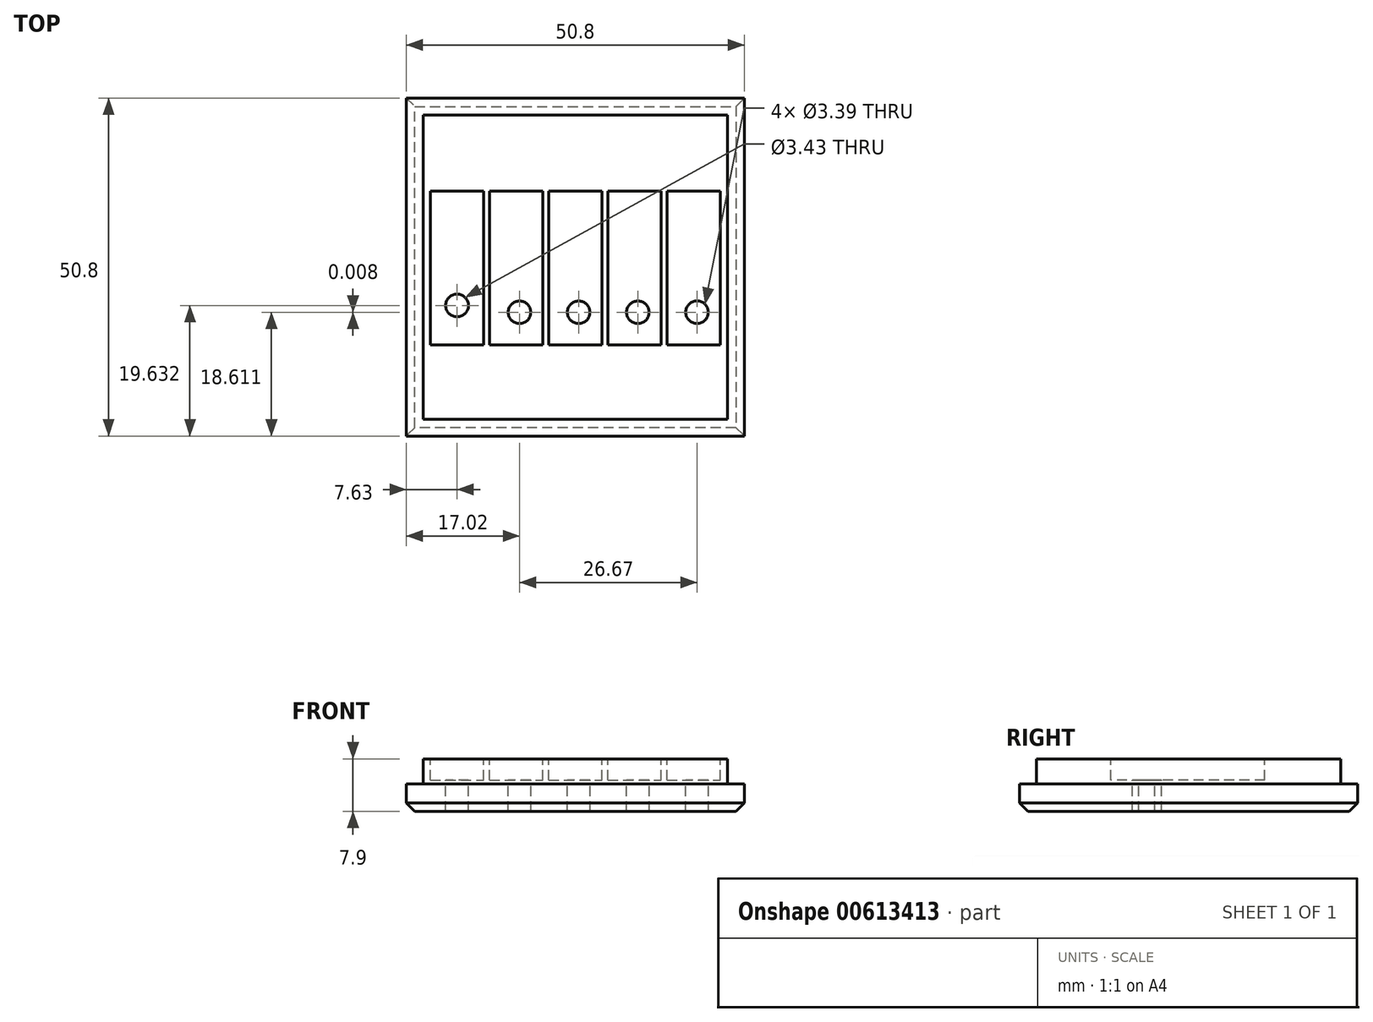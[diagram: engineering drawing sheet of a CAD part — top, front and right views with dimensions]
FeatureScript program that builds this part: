
annotation { "Feature Type Name" : "Feature", "Feature Type Description" : "" }
export const myFeature = defineFeature(function(context is Context, id is Id, definition is map)
    precondition{}
    {
        {
            var Q0;
            Q0=qCreatedBy(makeId("Top.planeOp"),FACE);
            var sketch = newSketch(context, id + "F0", { "sketchPlane" : qUnion([Q0])});
            skLineSegment(sketch, "E0.bottom", {"start": v(-12.32, 40.12) * mm, "end": v(38.48, 40.12) * mm});
            skLineSegment(sketch, "E0.top", {"start": v(-12.32, -10.68) * mm, "end": v(38.48, -10.68) * mm});
            skLineSegment(sketch, "E0.left", {"start": v(-12.32, 40.12) * mm, "end": v(-12.32, -10.68) * mm});
            skLineSegment(sketch, "E0.right", {"start": v(38.48, 40.12) * mm, "end": v(38.48, -10.68) * mm});
            skSolve(sketch);
        }
        {
            var Q0;
            Q0=makeQuery(id+"F0.imprint","IMPRINT",FACE,{"disambiguationData":[TD([[makeQuery(id+"F0.imprint","IMPRINT",EDGE,{"derivedFrom":sQuery(id+"F0.wireOp",EDGE,"E0.bottom")}),-1.0]])]});
            extrude(context, id + "F1", {"entities" : qUnion([Q0]), "depth" : 4.13 * mm, "offsetDistance" : 25.4 * mm});
        }
        {
            var Q0;
            Q0=makeQuery(id+"F1.opExtrude","CAP_FACE",FACE,{"disambiguationData":[OSD([sQuery(id+"F0.wireOp",EDGE,"E0.bottom"),sQuery(id+"F0.wireOp",EDGE,"E0.top"),sQuery(id+"F0.wireOp",EDGE,"E0.left"),sQuery(id+"F0.wireOp",EDGE,"E0.right")])],"isStart":true});
            var sketch = newSketch(context, id + "F2", { "sketchPlane" : qUnion([Q0])});
            skLineSegment(sketch, "E1.bottom", {"start": v(-10.03, 8.4) * mm, "end": v(36.2, 8.4) * mm});
            skLineSegment(sketch, "E1.top", {"start": v(-10.03, -37.84) * mm, "end": v(36.2, -37.84) * mm});
            skLineSegment(sketch, "E1.left", {"start": v(-10.03, 8.4) * mm, "end": v(-10.03, -37.84) * mm});
            skLineSegment(sketch, "E1.right", {"start": v(36.2, 8.4) * mm, "end": v(36.2, -37.84) * mm});
            skSolve(sketch);
        }
        {
            var Q0;
            Q0=makeQuery(id+"F1.opExtrude","CAP_FACE",FACE,{"disambiguationData":[OSD([sQuery(id+"F0.wireOp",EDGE,"E0.bottom"),sQuery(id+"F0.wireOp",EDGE,"E0.top"),sQuery(id+"F0.wireOp",EDGE,"E0.left"),sQuery(id+"F0.wireOp",EDGE,"E0.right")])],"isStart":false});
            var sketch = newSketch(context, id + "F3", { "sketchPlane" : qUnion([Q0])});
            skLineSegment(sketch, "E2.bottom", {"start": v(-9.78, 37.58) * mm, "end": v(35.94, 37.58) * mm});
            skLineSegment(sketch, "E2.top", {"start": v(-9.78, -8.14) * mm, "end": v(35.94, -8.14) * mm});
            skLineSegment(sketch, "E2.left", {"start": v(-9.78, 37.58) * mm, "end": v(-9.78, -8.14) * mm});
            skLineSegment(sketch, "E2.right", {"start": v(35.94, 37.58) * mm, "end": v(35.94, -8.14) * mm});
            skSolve(sketch);
        }
        {
            var Q0;
            Q0=makeQuery(id+"F3.imprint","IMPRINT",FACE,{"disambiguationData":[TD([[makeQuery(id+"F3.imprint","IMPRINT",EDGE,{"derivedFrom":sQuery(id+"F3.wireOp",EDGE,"E2.bottom")}),-1.0]])]});
            extrude(context, id + "F4", {"entities" : qUnion([Q0]), "operationType" : NewBodyOperationType.ADD, "depth" : 3.77 * mm, "offsetDistance" : 25.4 * mm});
        }
        {
            var Q0;
            Q0=makeQuery(id+"F4.opExtrude","CAP_FACE",FACE,{"disambiguationData":[OSD([sQuery(id+"F3.wireOp",EDGE,"E2.bottom"),sQuery(id+"F3.wireOp",EDGE,"E2.top"),sQuery(id+"F3.wireOp",EDGE,"E2.left"),sQuery(id+"F3.wireOp",EDGE,"E2.right")])],"isStart":false});
            var sketch = newSketch(context, id + "F5", { "sketchPlane" : qUnion([Q0])});
            skLineSegment(sketch, "E3.bottom", {"start": v(-8.69, 26.15) * mm, "end": v(-0.69, 26.15) * mm});
            skLineSegment(sketch, "E3.top", {"start": v(-8.69, 3.04) * mm, "end": v(-0.69, 3.04) * mm});
            skLineSegment(sketch, "E3.left", {"start": v(-8.69, 26.15) * mm, "end": v(-8.69, 3.04) * mm});
            skLineSegment(sketch, "E3.right", {"start": v(-0.69, 26.15) * mm, "end": v(-0.69, 3.04) * mm});
            skLineSegment(sketch, "E4.1.0.0", {"start": v(0.2, 26.15) * mm, "end": v(0.2, 3.04) * mm});
            skLineSegment(sketch, "E4.1.0.1", {"start": v(8.2, 26.15) * mm, "end": v(8.2, 3.04) * mm});
            skLineSegment(sketch, "E4.1.0.2", {"start": v(0.2, 26.15) * mm, "end": v(8.2, 26.15) * mm});
            skLineSegment(sketch, "E4.1.0.3", {"start": v(0.2, 3.04) * mm, "end": v(8.2, 3.04) * mm});
            skLineSegment(sketch, "E4.2.0.0", {"start": v(9.1, 26.15) * mm, "end": v(9.1, 3.04) * mm});
            skLineSegment(sketch, "E4.2.0.1", {"start": v(17.1, 26.15) * mm, "end": v(17.1, 3.04) * mm});
            skLineSegment(sketch, "E4.2.0.2", {"start": v(9.1, 26.15) * mm, "end": v(17.1, 26.15) * mm});
            skLineSegment(sketch, "E4.2.0.3", {"start": v(9.1, 3.04) * mm, "end": v(17.1, 3.04) * mm});
            skLineSegment(sketch, "E4.direction1", {"start": v(-8.69, 3.04) * mm, "end": v(0.2, 3.04) * mm, "construction": true});
            skLineSegment(sketch, "E4.direction2", {"start": v(-8.69, 3.04) * mm, "end": v(-8.69, 32.5) * mm, "construction": true});
            skLineSegment(sketch, "E5.0.3.0", {"start": v(17.98, 26.15) * mm, "end": v(17.98, 3.04) * mm});
            skLineSegment(sketch, "E5.3.3.0", {"start": v(25.98, 26.15) * mm, "end": v(25.98, 3.04) * mm});
            skLineSegment(sketch, "E5.6.3.0", {"start": v(17.98, 26.15) * mm, "end": v(25.98, 26.15) * mm});
            skLineSegment(sketch, "E5.9.3.0", {"start": v(17.98, 3.04) * mm, "end": v(25.98, 3.04) * mm});
            skLineSegment(sketch, "E5.0.4.0", {"start": v(26.87, 26.15) * mm, "end": v(26.87, 3.04) * mm});
            skLineSegment(sketch, "E5.3.4.0", {"start": v(34.87, 26.15) * mm, "end": v(34.87, 3.04) * mm});
            skLineSegment(sketch, "E5.6.4.0", {"start": v(26.87, 26.15) * mm, "end": v(34.87, 26.15) * mm});
            skLineSegment(sketch, "E5.9.4.0", {"start": v(26.87, 3.04) * mm, "end": v(34.87, 3.04) * mm});
            skSolve(sketch);
        }
        {
            var Q0;
            Q0=makeQuery(id+"F5.imprint","IMPRINT",FACE,{"disambiguationData":[TD([[makeQuery(id+"F5.imprint","IMPRINT",EDGE,{"derivedFrom":sQuery(id+"F5.wireOp",EDGE,"E4.1.0.0")}),1.0]])]});
            var Q1;
            Q1=makeQuery(id+"F5.imprint","IMPRINT",FACE,{"disambiguationData":[TD([[makeQuery(id+"F5.imprint","IMPRINT",EDGE,{"derivedFrom":sQuery(id+"F5.wireOp",EDGE,"E4.2.0.0")}),1.0]])]});
            var Q2;
            Q2=makeQuery(id+"F5.imprint","IMPRINT",FACE,{"disambiguationData":[TD([[makeQuery(id+"F5.imprint","IMPRINT",EDGE,{"derivedFrom":sQuery(id+"F5.wireOp",EDGE,"E5.0.3.0")}),1.0]])]});
            var Q3;
            Q3=makeQuery(id+"F5.imprint","IMPRINT",FACE,{"disambiguationData":[TD([[makeQuery(id+"F5.imprint","IMPRINT",EDGE,{"derivedFrom":sQuery(id+"F5.wireOp",EDGE,"E5.0.4.0")}),1.0]])]});
            var Q4;
            Q4=makeQuery(id+"F5.imprint","IMPRINT",FACE,{"disambiguationData":[TD([[makeQuery(id+"F5.imprint","IMPRINT",EDGE,{"derivedFrom":sQuery(id+"F5.wireOp",EDGE,"E3.bottom")}),-1.0]])]});
            extrude(context, id + "F6", {"entities" : qUnion([Q0, Q1, Q2, Q3, Q4]), "operationType" : NewBodyOperationType.REMOVE, "oppositeDirection" : true, "depth" : 3.2 * mm, "offsetDistance" : 25.4 * mm});
        }
        {
            var Q0;
            Q0=makeQuery(id+"F6.boolean.opBoolean","COPY",FACE,{"derivedFrom":makeQuery(id+"F6.opExtrude","CAP_FACE",FACE,{"disambiguationData":[OSD([sQuery(id+"F5.wireOp",EDGE,"E3.bottom"),sQuery(id+"F5.wireOp",EDGE,"E3.top"),sQuery(id+"F5.wireOp",EDGE,"E3.left"),sQuery(id+"F5.wireOp",EDGE,"E3.right")])],"isStart":false})});
            var sketch = newSketch(context, id + "F7", { "sketchPlane" : qUnion([Q0])});
            skCircle(sketch, "E6", {"center": v(-4.69, 8.95) * mm, "radius": 1.71 * mm});
            skLineSegment(sketch, "E7.bottom", {"start": v(3.2, -6.76) * mm, "end": v(26.27, -6.76) * mm});
            skLineSegment(sketch, "E7.top", {"start": v(3.2, 1.24) * mm, "end": v(26.27, 1.24) * mm});
            skLineSegment(sketch, "E7.left", {"start": v(3.2, -6.76) * mm, "end": v(3.2, 1.24) * mm});
            skLineSegment(sketch, "E7.right", {"start": v(26.27, -6.76) * mm, "end": v(26.27, 1.24) * mm});
            skLineSegment(sketch, "E8.bottom", {"start": v(3.1, 3.08) * mm, "end": v(26.16, 3.08) * mm});
            skLineSegment(sketch, "E8.top", {"start": v(3.1, 11.08) * mm, "end": v(26.16, 11.08) * mm});
            skLineSegment(sketch, "E8.left", {"start": v(3.1, 3.08) * mm, "end": v(3.1, 11.08) * mm});
            skLineSegment(sketch, "E8.right", {"start": v(26.16, 3.08) * mm, "end": v(26.16, 11.08) * mm});
            skCircle(sketch, "E9", {"center": v(21.41, -2.74) * mm, "radius": 1.71 * mm});
            skCircle(sketch, "E10", {"center": v(21.31, 7.1) * mm, "radius": 1.71 * mm});
            skSolve(sketch);
        }
        {
            var Q0;
            Q0=makeQuery(id+"F7.imprint","IMPRINT",FACE,{"disambiguationData":[TD([[makeQuery(id+"F7.imprint","IMPRINT",EDGE,{"derivedFrom":sQuery(id+"F7.wireOp",EDGE,"E6")}),1.0]])]});
            var Q1;
            Q1=qSketchRegion(id+"F10",true);
            extrude(context, id + "F8", {"entities" : qUnion([Q0, Q1]), "operationType" : NewBodyOperationType.REMOVE, "oppositeDirection" : true, "depth" : 25.4 * mm, "offsetDistance" : 25.4 * mm});
        }
        {
            var Q0;
            Q0=makeQuery(id+"F1.opExtrude","CAP_EDGE",EDGE,{"disambiguationData":[OSD([sQuery(id+"F0.wireOp",EDGE,"E0.top")])],"isStart":true});
            var Q1;
            Q1=makeQuery(id+"F1.opExtrude","CAP_EDGE",EDGE,{"disambiguationData":[OSD([sQuery(id+"F0.wireOp",EDGE,"E0.bottom")])],"isStart":true});
            var Q2;
            Q2=makeQuery(id+"F1.opExtrude","CAP_EDGE",EDGE,{"disambiguationData":[OSD([sQuery(id+"F0.wireOp",EDGE,"E0.left")])],"isStart":true});
            var Q3;
            Q3=makeQuery(id+"F1.opExtrude","CAP_EDGE",EDGE,{"disambiguationData":[OSD([sQuery(id+"F0.wireOp",EDGE,"E0.right")])],"isStart":true});
            chamfer(context, id + "F9", {"entities" : qUnion([Q0, Q1, Q2, Q3]), "width" : 1.27 * mm, "tangentPropagation" : true});
        }
        {
            var Q0;
            Q0=makeQuery(id+"F6.boolean.opBoolean","COPY",FACE,{"derivedFrom":makeQuery(id+"F6.opExtrude","CAP_FACE",FACE,{"disambiguationData":[OSD([sQuery(id+"F5.wireOp",EDGE,"E4.1.0.0"),sQuery(id+"F5.wireOp",EDGE,"E4.1.0.1"),sQuery(id+"F5.wireOp",EDGE,"E4.1.0.2"),sQuery(id+"F5.wireOp",EDGE,"E4.1.0.3")])],"isStart":false})});
            var sketch = newSketch(context, id + "F10", { "sketchPlane" : qUnion([Q0])});
            skCircle(sketch, "E11", {"center": v(4.7, 7.93) * mm, "radius": 1.7 * mm});
            skCircle(sketch, "E12", {"center": v(13.6, 7.93) * mm, "radius": 1.7 * mm});
            skCircle(sketch, "E13", {"center": v(22.48, 7.93) * mm, "radius": 1.7 * mm});
            skCircle(sketch, "E14", {"center": v(31.37, 7.94) * mm, "radius": 1.7 * mm});
            skSolve(sketch);
        }
        {
            var Q0;
            Q0=makeQuery(id+"F10.imprint","IMPRINT",FACE,{"disambiguationData":[TD([[makeQuery(id+"F10.imprint","IMPRINT",EDGE,{"derivedFrom":sQuery(id+"F10.wireOp",EDGE,"E11")}),1.0]])]});
            var Q1;
            Q1=makeQuery(id+"F10.imprint","IMPRINT",FACE,{"disambiguationData":[TD([[makeQuery(id+"F10.imprint","IMPRINT",EDGE,{"derivedFrom":sQuery(id+"F10.wireOp",EDGE,"E12")}),1.0]])]});
            var Q2;
            Q2=makeQuery(id+"F10.imprint","IMPRINT",FACE,{"disambiguationData":[TD([[makeQuery(id+"F10.imprint","IMPRINT",EDGE,{"derivedFrom":sQuery(id+"F10.wireOp",EDGE,"E13")}),1.0]])]});
            var Q3;
            Q3=makeQuery(id+"F10.imprint","IMPRINT",FACE,{"disambiguationData":[TD([[makeQuery(id+"F10.imprint","IMPRINT",EDGE,{"derivedFrom":sQuery(id+"F10.wireOp",EDGE,"E14")}),1.0]])]});
            extrude(context, id + "F11", {"entities" : qUnion([Q0, Q1, Q2, Q3]), "operationType" : NewBodyOperationType.REMOVE, "oppositeDirection" : true, "depth" : 25.4 * mm, "offsetDistance" : 25.4 * mm});
        }
    });
